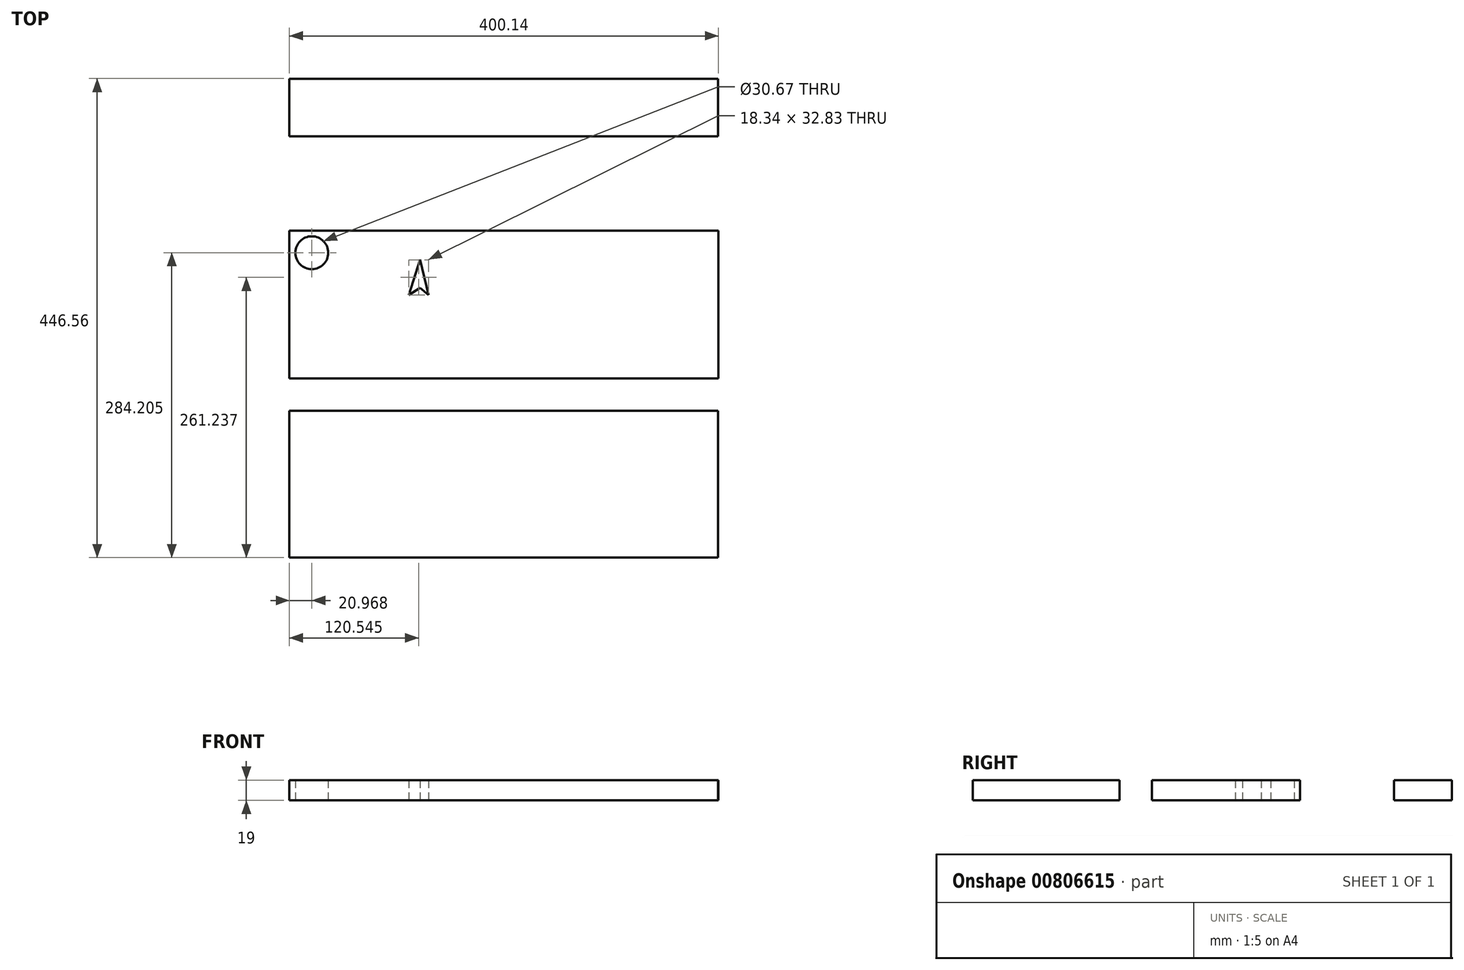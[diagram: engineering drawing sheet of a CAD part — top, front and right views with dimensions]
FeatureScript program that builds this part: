
annotation { "Feature Type Name" : "Feature", "Feature Type Description" : "" }
export const myFeature = defineFeature(function(context is Context, id is Id, definition is map)
    precondition{}
    {
        {
            var Q0;
            Q0=qCreatedBy(makeId("Top.planeOp"),FACE);
            var sketch = newSketch(context, id + "F0", { "sketchPlane" : qUnion([Q0])});
            skLineSegment(sketch, "E0.bottom", {"start": v(-66.23, 60.1) * mm, "end": v(-466.37, 60.1) * mm});
            skLineSegment(sketch, "E0.top", {"start": v(-66.23, -77.8) * mm, "end": v(-466.37, -77.8) * mm});
            skLineSegment(sketch, "E0.left", {"start": v(-66.23, 60.1) * mm, "end": v(-66.23, -77.8) * mm});
            skLineSegment(sketch, "E0.right", {"start": v(-466.37, 60.1) * mm, "end": v(-466.37, -77.8) * mm});
            skLineSegment(sketch, "E1.bottom", {"start": v(-466.37, -107.93) * mm, "end": v(-66.75, -107.93) * mm});
            skLineSegment(sketch, "E1.top", {"start": v(-466.37, -244.82) * mm, "end": v(-66.75, -244.82) * mm});
            skLineSegment(sketch, "E1.left", {"start": v(-466.37, -107.93) * mm, "end": v(-466.37, -244.82) * mm});
            skLineSegment(sketch, "E1.right", {"start": v(-66.75, -107.93) * mm, "end": v(-66.75, -244.82) * mm});
            skLineSegment(sketch, "E2.bottom", {"start": v(-466.37, 201.74) * mm, "end": v(-66.75, 201.74) * mm});
            skLineSegment(sketch, "E2.top", {"start": v(-466.37, 148) * mm, "end": v(-66.75, 148) * mm});
            skLineSegment(sketch, "E2.left", {"start": v(-466.37, 201.74) * mm, "end": v(-466.37, 148) * mm});
            skLineSegment(sketch, "E2.right", {"start": v(-66.75, 201.74) * mm, "end": v(-66.75, 148) * mm});
            skCircle(sketch, "E3", {"center": v(-445.4, 39.38) * mm, "radius": 15.34 * mm});
            skLineSegment(sketch, "E4", {"start": v(-344.52, 32.83) * mm, "end": v(-355, 0) * mm});
            skLineSegment(sketch, "E5", {"start": v(-355, 0) * mm, "end": v(-344.52, 32.83) * mm});
            skLineSegment(sketch, "E6", {"start": v(-344.52, 32.83) * mm, "end": v(-336.65, 0) * mm});
            skLineSegment(sketch, "E7", {"start": v(-336.65, 0) * mm, "end": v(-344.52, 6.63) * mm});
            skLineSegment(sketch, "E8", {"start": v(-344.52, 6.63) * mm, "end": v(-355, 0) * mm});
            skLineSegment(sketch, "E9", {"start": v(-336.65, 0) * mm, "end": v(-344.52, -9.32) * mm});
            skLineSegment(sketch, "E10", {"start": v(-344.52, -9.32) * mm, "end": v(-355, 0) * mm});
            skLineSegment(sketch, "E11", {"start": v(-344.52, -9.32) * mm, "end": v(-344.52, -22.2) * mm});
            skCircle(sketch, "E12", {"center": v(-344.52, -28.75) * mm, "radius": 7.97 * mm});
            skLineSegment(sketch, "E13", {"start": v(-284.24, 32.83) * mm, "end": v(-297.35, 0) * mm});
            skLineSegment(sketch, "E14", {"start": v(-297.35, 0) * mm, "end": v(-323.55, -14.33) * mm});
            skLineSegment(sketch, "E15", {"start": v(-323.55, -14.33) * mm, "end": v(-297.35, -24.8) * mm});
            skLineSegment(sketch, "E16", {"start": v(-297.35, -24.8) * mm, "end": v(-284.24, -53.64) * mm});
            skLineSegment(sketch, "E17", {"start": v(-284.24, -53.64) * mm, "end": v(-272.25, -23.59) * mm});
            skLineSegment(sketch, "E18", {"start": v(-272.25, -23.59) * mm, "end": v(-246.25, -14.33) * mm});
            skLineSegment(sketch, "E19", {"start": v(-246.25, -14.33) * mm, "end": v(-272.25, 0) * mm});
            skLineSegment(sketch, "E20", {"start": v(-272.25, 0) * mm, "end": v(-284.24, 32.83) * mm});
            skCircle(sketch, "E21", {"center": v(-284.24, -10.4) * mm, "radius": 10.23 * mm});
            skSolve(sketch);
        }
        {
            var Q0;
            Q0=makeQuery(id+"F0.imprint","IMPRINT",FACE,{"disambiguationData":[TD([[makeQuery(id+"F0.imprint","IMPRINT",EDGE,{"derivedFrom":sQuery(id+"F0.wireOp",EDGE,"E1.bottom")}),-1.0]])]});
            var Q1;
            Q1=makeQuery(id+"F0.imprint","IMPRINT",FACE,{"disambiguationData":[TD([[makeQuery(id+"F0.imprint","IMPRINT",EDGE,{"derivedFrom":sQuery(id+"F0.wireOp",EDGE,"E2.bottom")}),-1.0]])]});
            var Q2;
            Q2=makeQuery(id+"F0.imprint","IMPRINT",FACE,{"disambiguationData":[TD([[makeQuery(id+"F0.imprint","IMPRINT",EDGE,{"derivedFrom":sQuery(id+"F0.wireOp",EDGE,"E0.bottom")}),1.0]])]});
            var Q3;
            Q3=makeQuery(id+"F0.imprint","IMPRINT",FACE,{"disambiguationData":[TD([[makeQuery(id+"F0.imprint","IMPRINT",EDGE,{"derivedFrom":sQuery(id+"F0.wireOp",EDGE,"E12")}),1.0]])]});
            var Q4;
            Q4=makeQuery(id+"F0.imprint","IMPRINT",FACE,{"disambiguationData":[TD([[makeQuery(id+"F0.imprint","IMPRINT",EDGE,{"derivedFrom":sQuery(id+"F0.wireOp",EDGE,"E7")}),1.0]])]});
            var Q5;
            Q5=makeQuery(id+"F0.imprint","IMPRINT",FACE,{"disambiguationData":[TD([[makeQuery(id+"F0.imprint","IMPRINT",EDGE,{"derivedFrom":sQuery(id+"F0.wireOp",EDGE,"E5")}),-1.0]])]});
            var Q6;
            Q6=makeQuery(id+"F0.imprint","IMPRINT",FACE,{"disambiguationData":[TD([[makeQuery(id+"F0.imprint","IMPRINT",EDGE,{"derivedFrom":sQuery(id+"F0.wireOp",EDGE,"E13")}),1.0]])]});
            var Q7;
            Q7=makeQuery(id+"F0.imprint","IMPRINT",FACE,{"disambiguationData":[TD([[makeQuery(id+"F0.imprint","IMPRINT",EDGE,{"derivedFrom":sQuery(id+"F0.wireOp",EDGE,"E21")}),1.0]])]});
            extrude(context, id + "F1", {"entities" : qUnion([Q0, Q1, Q2, Q3, Q4, Q5, Q6, Q7]), "depth" : 19 * mm, "offsetDistance" : 25 * mm});
        }
    });
